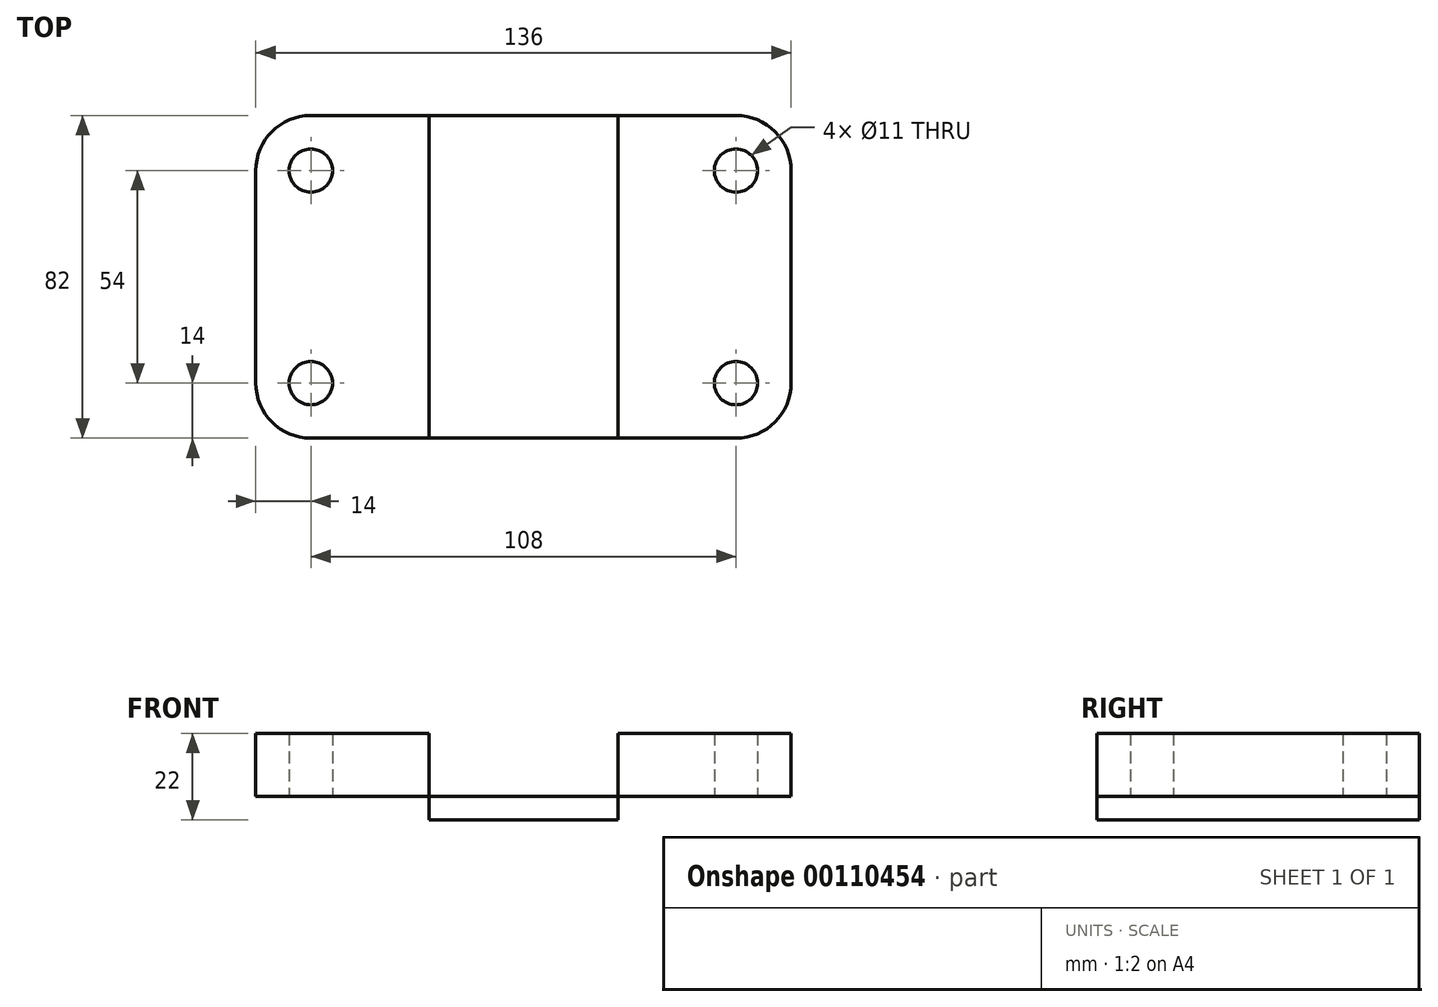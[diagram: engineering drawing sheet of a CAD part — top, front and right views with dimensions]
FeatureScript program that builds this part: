
annotation { "Feature Type Name" : "Feature", "Feature Type Description" : "" }
export const myFeature = defineFeature(function(context is Context, id is Id, definition is map)
    precondition{}
    {
        {
            var Q0;
            Q0=qCreatedBy(makeId("Top.planeOp"),FACE);
            var sketch = newSketch(context, id + "F0", { "sketchPlane" : qUnion([Q0])});
            skLineSegment(sketch, "E0.bottom", {"start": v(54, -41) * mm, "end": v(-54, -41) * mm});
            skLineSegment(sketch, "E0.top", {"start": v(54, 41) * mm, "end": v(-54, 41) * mm});
            skLineSegment(sketch, "E0.left", {"start": v(68, -27) * mm, "end": v(68, 27) * mm});
            skLineSegment(sketch, "E0.right", {"start": v(-68, -27) * mm, "end": v(-68, 27) * mm});
            skPoint(sketch, "E0.middle", {"position": v(0, 0) * mm});
            skPoint(sketch, "E1.visualSharp", {"position": v(-68, 41) * mm});
            skArc(sketch, "E1.filletArc", {"start": v(-54, 41) * mm, "mid": v(-63.9, 36.9) * mm, "end": v(-68, 27) * mm});
            skPoint(sketch, "E2.visualSharp", {"position": v(68, 41) * mm});
            skArc(sketch, "E2.filletArc", {"start": v(68, 27) * mm, "mid": v(63.9, 36.9) * mm, "end": v(54, 41) * mm});
            skPoint(sketch, "E3.visualSharp", {"position": v(68, -41) * mm});
            skArc(sketch, "E3.filletArc", {"start": v(54, -41) * mm, "mid": v(63.9, -36.9) * mm, "end": v(68, -27) * mm});
            skPoint(sketch, "E4.visualSharp", {"position": v(-68, -41) * mm});
            skArc(sketch, "E4.filletArc", {"start": v(-68, -27) * mm, "mid": v(-63.9, -36.9) * mm, "end": v(-54, -41) * mm});
            skCircle(sketch, "E5", {"center": v(-54, 27) * mm, "radius": 5.5 * mm});
            skCircle(sketch, "E6", {"center": v(-54, -27) * mm, "radius": 5.5 * mm});
            skCircle(sketch, "E7", {"center": v(54, -27) * mm, "radius": 5.5 * mm});
            skCircle(sketch, "E8", {"center": v(54, 27) * mm, "radius": 5.5 * mm});
            skLineSegment(sketch, "E9", {"start": v(-54, 41) * mm, "end": v(-54, -54.77) * mm, "construction": true});
            skLineSegment(sketch, "E10", {"start": v(54, 41) * mm, "end": v(54, -54.77) * mm, "construction": true});
            skLineSegment(sketch, "E11", {"start": v(-71.37, 27) * mm, "end": v(81.66, 27) * mm, "construction": true});
            skLineSegment(sketch, "E12", {"start": v(-71.67, -27) * mm, "end": v(81.66, -27) * mm, "construction": true});
            skSolve(sketch);
        }
        {
            var Q0;
            Q0 = qSketchRegion(id + "F0", true);
            extrude(context, id + "F1", {"entities" : qUnion([Q0]), "depth" : 16 * mm});
        }
        {
            var Q0;
            Q0=qCreatedBy(makeId("Top.planeOp"),FACE);
            var sketch = newSketch(context, id + "F2", { "sketchPlane" : qUnion([Q0])});
            skLineSegment(sketch, "E13.bottom", {"start": v(24, -41) * mm, "end": v(-24, -41) * mm});
            skLineSegment(sketch, "E13.top", {"start": v(24, 41) * mm, "end": v(-24, 41) * mm});
            skLineSegment(sketch, "E13.left", {"start": v(24, -41) * mm, "end": v(24, 41) * mm});
            skLineSegment(sketch, "E13.right", {"start": v(-24, -41) * mm, "end": v(-24, 41) * mm});
            skPoint(sketch, "E13.middle", {"position": v(0, 0) * mm});
            skSolve(sketch);
        }
        {
            var Q0;
            Q0 = qSketchRegion(id + "F2", true);
            extrude(context, id + "F3", {"entities" : qUnion([Q0]), "operationType" : NewBodyOperationType.ADD, "oppositeDirection" : true, "depth" : 6 * mm});
        }
        {
            var Q0;
            Q0=qCreatedBy(makeId("Top.planeOp"),FACE);
            var sketch = newSketch(context, id + "F4", { "sketchPlane" : qUnion([Q0])});
            skLineSegment(sketch, "E14.bottom", {"start": v(24, 41) * mm, "end": v(-24, 41) * mm});
            skLineSegment(sketch, "E14.top", {"start": v(24, -41) * mm, "end": v(-24, -41) * mm});
            skLineSegment(sketch, "E14.left", {"start": v(24, 41) * mm, "end": v(24, -41) * mm});
            skLineSegment(sketch, "E14.right", {"start": v(-24, 41) * mm, "end": v(-24, -41) * mm});
            skPoint(sketch, "E14.middle", {"position": v(0, 0) * mm});
            skSolve(sketch);
        }
        {
            var Q0;
            Q0 = qSketchRegion(id + "F4", true);
            extrude(context, id + "F5", {"entities" : qUnion([Q0]), "operationType" : NewBodyOperationType.REMOVE, "endBound" : BoundingType.UP_TO_NEXT, "depth" : 6 * mm});
        }
    });
